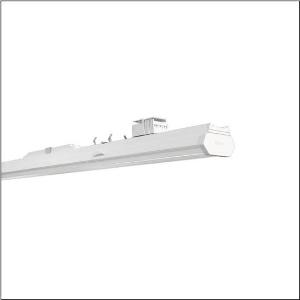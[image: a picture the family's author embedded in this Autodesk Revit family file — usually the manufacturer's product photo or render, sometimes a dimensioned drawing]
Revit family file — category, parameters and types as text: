
# Revit family: licross_r__21_protected_mo_52td1bmn4axg_a5a6
name_source: partatom
category: Lighting Fixtures
units: mm (PartAtom-declared; Revit-internal decimal feet)

## family parameters
Cut with Voids When Loaded = No
Host = Face
Light Source = No
Part Type = Normal
Room Calculation Point = No
Round Connector Dimension = Use Diameter
Shared = No

## types (1)
- --- (1 x LED, 10100 lm, 60.5 W, 4000K)
    Apparent Load = 61 VA
    CIE Flux Codes = 54 82 95 97 100
    Color Rendering = 80
    Color Temperature = 4000K
    Default Elevation = 1800 mm
    Description = Licross® 21 Protected MO, luminaire insert, of sheet steel, galvanised, coil coated, white, length: 1.500mm, width: 90mm, height: 103mm, LED rated luminous flux: 10.100lm, light colour: 840, control gear: ON/OFF Multilumen, with plug, 3-pole, with phase selection, mains connection: 220..240V, AC, 50/60Hz, rated input power: 61W, halogen-free wiring, primary optical cover: cover, of PMMA, light emission: direct distribution, primary light characteristic: symmetric, protection rating (complete): IP54, insulation class (complete): insulation class I (protective earthing), certification: CE, ENEC, VDE, UKCA, protection symbol: D if used in an environment with non-conductive dust loads with corresponding accessories, impact resistance: IK06, permissible ambient temperature for indoor applications: -35..+45°C, corresponds to IFS (International Featured Standards) requirements for safety and quality in the food industry, reducing of maximum allowable ambient temperature of 5°C with ceiling mounting, LABS conformity tested according to VDMA 24364:2018-05, packaging unit: 1 piece
    Height = 92 mm
    Lamp = 1 x LED
    Lamp Light Flux = 10100 lm
    Lamp Power = 60.5 W
    Lamp count = 1
    Length = 1500 mm
    Luminous efficacy = 167 lm/W
    Manufacturer = Siteco
    ModVariant = No
    Model = 52TD1BMN4AXG
    Mounting Place = Ceiling
    Mounting Type = Pendant
    Number of Poles = 1
    OnlyDefault = Yes
    Power Factor = 1
    Product Name = Licross® 21 Protected MO
    Product group = luminaire insert
    ProductGroupID = 901
    Protection Class = Protection class I
    Protection Degree = IP 54
    RLX_Detail_Level = 1
    RLX_Emergency_Light_Flux = 0 lm
    RLX_Emergency_Type = 0
    RLX_Emergency_Type_DB = No
    RlxData = <blob elided: 22125 chars, md5=8d87311b>
    Socket = socket
    Standby Power = 0 W
    System Light Flux = 10100 lm
    System Power = 61 W
    Type Comments = factory setting: luminous flux: 100 % | (A | C | E) | 140 mA
    Type Image = l_1256148.jpg
    URL = http://relux.com
    VarID = @adj_039319
    Voltage = 0 V
    Weight = 0.00 kg
    Width = 88 mm

## geometry (parser evidence)
native form markers: Blend x4, Sweep x10
no freeform markers — native parametric forms only
